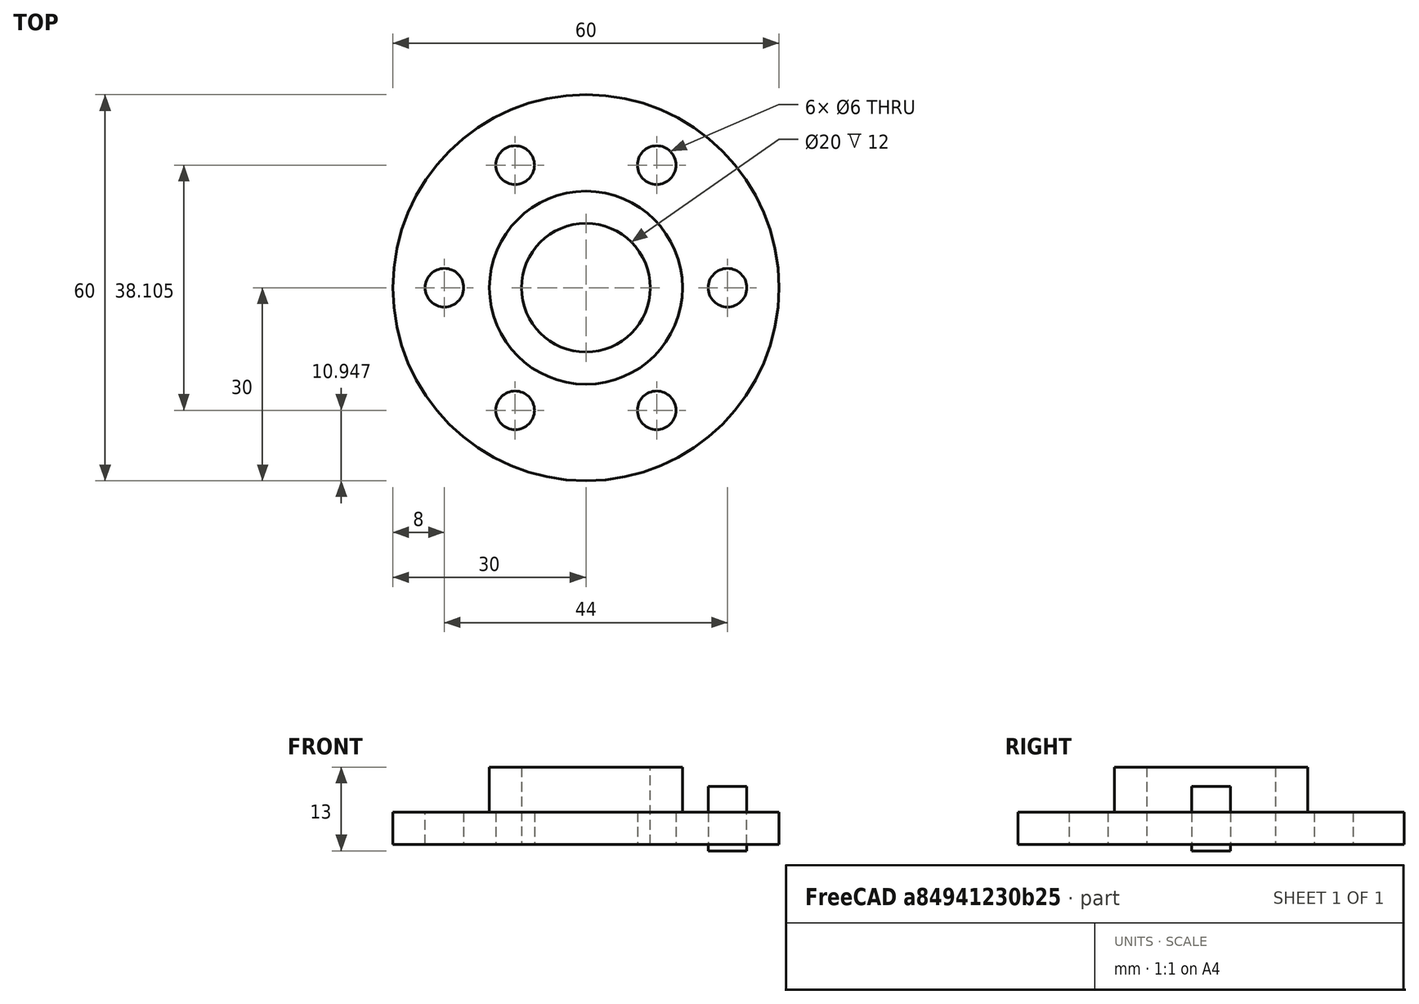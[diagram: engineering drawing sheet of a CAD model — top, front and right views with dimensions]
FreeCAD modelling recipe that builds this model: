
FCSTD DOCUMENT  (FreeCAD 0.21R33694 (Git))
Label: OJT1_T011P010_brida
License: All rights reserved
LicenseURL: http://en.wikipedia.org/wiki/All_rights_reserved
objects: Part::Cylinder×4, Part::Cut×2, Part::MultiFuse×1, Part::FeaturePython×1
note: 7 computed .brp shape members not serialized (recipe doc carries the construction recipe); baked Part::Feature solids carry a one-line shape summary decoded from their .brp

FEATURE [Part::Cylinder] Cylinder  label="base"
  Angle = 360
  AttacherType = Attacher::AttachEngine3D
  FirstAngle = 0
  Height = 5
  Radius = 30
  SecondAngle = 0
FEATURE [Part::Cylinder] Cylinder001  label="tub_exterior"
  Angle = 360
  AttacherType = Attacher::AttachEngine3D
  FirstAngle = 0
  Height = 12
  Radius = 15
  SecondAngle = 0
FEATURE [Part::MultiFuse] Fusion
  Refine = true
  Shapes = -> [Cylinder,Cylinder001]
FEATURE [Part::Cylinder] Cylinder002  label="tub_interior"
  Angle = 360
  AttacherType = Attacher::AttachEngine3D
  FirstAngle = 0
  Height = 30
  Placement = pos=(0,0,-1) rot=(0,0,1;0rad)
  Radius = 10
  SecondAngle = 0
FEATURE [Part::Cut] Cut  label="brida_sense_forats"
  Base = -> Fusion
  Refine = true
  Tool = -> Cylinder002
FEATURE [Part::Cylinder] Cylinder003  label="taladro_master"
  Angle = 360
  AttacherType = Attacher::AttachEngine3D
  FirstAngle = 0
  Height = 10
  Placement = pos=(22,0,-1) rot=(0,0,1;0rad)
  Radius = 3
  SecondAngle = 0
FEATURE [Part::FeaturePython] Array  # Draft array (typed FeaturePython)
  AlwaysSyncPlacement = false
  Angle = 360
  ArrayType = 1
  Axis = (0,0,1)
  Base = -> Cylinder003
  Center = (0,0,0)
  Count = 6
  ExpandArray = false
  Fuse = false
  IntervalAxis = (0,0,0)
  IntervalX = (100,0,0)
  IntervalY = (0,100,0)
  IntervalZ = (0,0,100)
  NumberCircles = 3
  NumberPolar = 6
  NumberX = 2
  NumberY = 2
  NumberZ = 1
  PlacementList = 6 placements: [(22,0,-1),(11,19.0526,-1),(-11,19.0526,-1),(-22,2.69422e-15,-1),(-11,-19.0526,-1),(11,-19.0526,-1)]
  RadialDistance = 50
  ScaleList = (6) [(1,1,1),(1,1,1),(1,1,1),(1,1,1),(1,1,1),(1,1,1)]
  Symmetry = 1
  TangentialDistance = 25
FEATURE [Part::Cut] Cut001
  Base = -> Cut
  Refine = true
  Tool = -> Array
